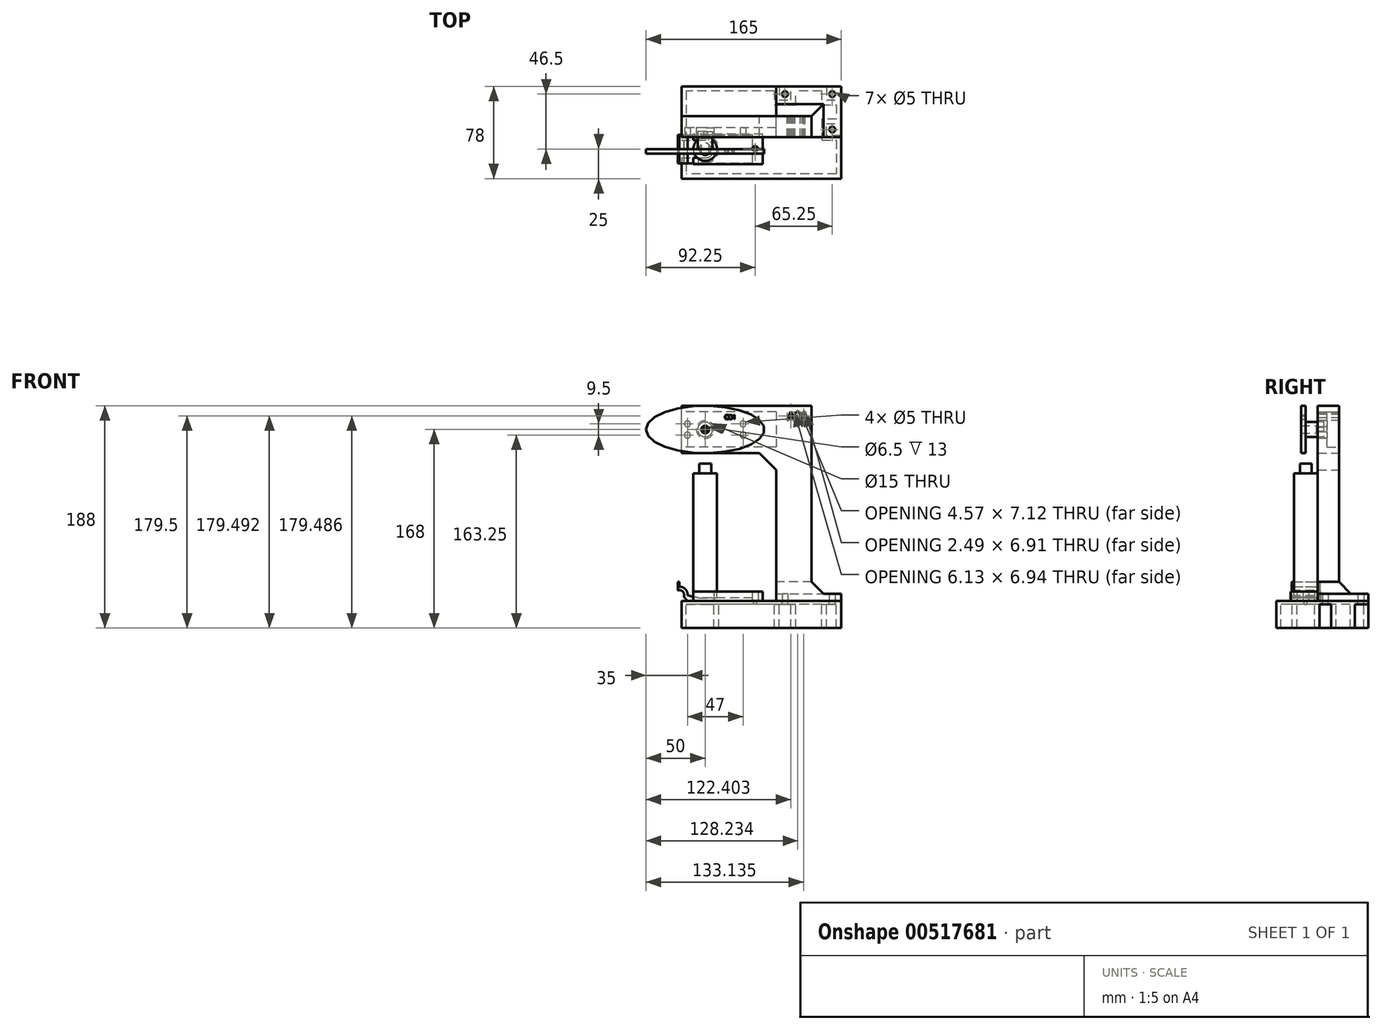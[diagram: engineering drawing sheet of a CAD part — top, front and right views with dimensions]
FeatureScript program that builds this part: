
annotation { "Feature Type Name" : "Feature", "Feature Type Description" : "" }
export const myFeature = defineFeature(function(context is Context, id is Id, definition is map)
    precondition{}
    {
        {
            var Q0;
            Q0=qCreatedBy(makeId("Front.planeOp"),FACE);
            var sketch = newSketch(context, id + "F0", { "sketchPlane" : qUnion([Q0])});
            skLineSegment(sketch, "E0", {"start": v(0, 0) * mm, "end": v(0, 110.86) * mm});
            skLineSegment(sketch, "E1", {"start": v(0, 110.86) * mm, "end": v(-14.14, 125) * mm});
            skLineSegment(sketch, "E2", {"start": v(-14.14, 125) * mm, "end": v(-80, 125) * mm});
            skLineSegment(sketch, "E3", {"start": v(-80, 125) * mm, "end": v(-80, 165) * mm});
            skLineSegment(sketch, "E4", {"start": v(-80, 165) * mm, "end": v(30, 165) * mm});
            skLineSegment(sketch, "E5", {"start": v(30, 165) * mm, "end": v(30, 0) * mm});
            skLineSegment(sketch, "E6", {"start": v(30, 0) * mm, "end": v(0, 0) * mm});
            skLineSegment(sketch, "E7", {"start": v(-14.14, 125) * mm, "end": v(0, 125) * mm, "construction": true});
            skLineSegment(sketch, "E8", {"start": v(0, 125) * mm, "end": v(0, 110.86) * mm, "construction": true});
            skText(sketch, "E9", { "text": "A01", "fontName": "OpenSans-Regular.ttf"});
            skLineSegment(sketch, "E10", {"start": v(25, 165) * mm, "end": v(25, 160) * mm, "construction": true});
            skLineSegment(sketch, "E11", {"start": v(25, 160) * mm, "end": v(30, 160) * mm, "construction": true});
            const initialGuessF0  = {"E9": [0.00934, 0.15303, 1, 0, 0.00697]};
            skSetInitialGuess(sketch, initialGuessF0);
            skSolve(sketch);
        }
        {
            var Q0;
            Q0=qSketchRegion(id+"F0",true);
            extrude(context, id + "F1", {"entities" : qUnion([Q0]), "depth" : 18 * mm, "offsetDistance" : 25 * mm});
        }
        {
            var Q0;
            Q0=makeQuery(id+"F1.opExtrude","CAP_FACE",FACE,{"disambiguationData":[OSD([sQuery(id+"F0.wireOp",EDGE,"E0"),sQuery(id+"F0.wireOp",EDGE,"E1"),sQuery(id+"F0.wireOp",EDGE,"E2"),sQuery(id+"F0.wireOp",EDGE,"E3"),sQuery(id+"F0.wireOp",EDGE,"E4"),sQuery(id+"F0.wireOp",EDGE,"E5"),sQuery(id+"F0.wireOp",EDGE,"E6")])],"isStart":false});
            var sketch = newSketch(context, id + "F2", { "sketchPlane" : qUnion([Q0])});
            skCircle(sketch, "E12", {"center": v(-75, 149.75) * mm, "radius": 2.5 * mm});
            skCircle(sketch, "E13", {"center": v(-75, 140.25) * mm, "radius": 2.5 * mm});
            skCircle(sketch, "E14", {"center": v(-28, 140.25) * mm, "radius": 2.5 * mm});
            skCircle(sketch, "E15", {"center": v(-28, 149.75) * mm, "radius": 2.5 * mm});
            skCircle(sketch, "E16", {"center": v(-60, 145) * mm, "radius": 7.5 * mm});
            skLineSegment(sketch, "E17", {"start": v(-75, 149.75) * mm, "end": v(-60, 149.75) * mm, "construction": true});
            skLineSegment(sketch, "E18", {"start": v(-60, 149.75) * mm, "end": v(-60, 145) * mm, "construction": true});
            skLineSegment(sketch, "E19", {"start": v(-75, 140.25) * mm, "end": v(-60, 140.25) * mm, "construction": true});
            skLineSegment(sketch, "E20", {"start": v(-60, 140.25) * mm, "end": v(-60, 145) * mm, "construction": true});
            skSolve(sketch);
        }
        {
            var Q0;
            Q0=qSketchRegion(id+"F2",true);
            extrude(context, id + "F3", {"entities" : qUnion([Q0]), "operationType" : NewBodyOperationType.REMOVE, "endBound" : BoundingType.THROUGH_ALL, "oppositeDirection" : true, "depth" : 25 * mm, "offsetDistance" : 25 * mm});
        }
        {
            var Q0;
            Q0=makeQuery(id+"F1.opExtrude","CAP_FACE",FACE,{"disambiguationData":[OSD([sQuery(id+"F0.wireOp",EDGE,"E0"),sQuery(id+"F0.wireOp",EDGE,"E1"),sQuery(id+"F0.wireOp",EDGE,"E2"),sQuery(id+"F0.wireOp",EDGE,"E3"),sQuery(id+"F0.wireOp",EDGE,"E4"),sQuery(id+"F0.wireOp",EDGE,"E5"),sQuery(id+"F0.wireOp",EDGE,"E6")])],"isStart":true});
            var sketch = newSketch(context, id + "F4", { "sketchPlane" : qUnion([Q0])});
            skLineSegment(sketch, "E21.bottom", {"start": v(0, 160) * mm, "end": v(80, 160) * mm});
            skLineSegment(sketch, "E21.top", {"start": v(0, 130) * mm, "end": v(80, 130) * mm});
            skLineSegment(sketch, "E21.left", {"start": v(0, 160) * mm, "end": v(0, 130) * mm});
            skLineSegment(sketch, "E21.right", {"start": v(80, 160) * mm, "end": v(80, 130) * mm});
            skSolve(sketch);
        }
        {
            var Q0;
            Q0=qSketchRegion(id+"F4",true);
            extrude(context, id + "F5", {"entities" : qUnion([Q0]), "operationType" : NewBodyOperationType.REMOVE, "oppositeDirection" : true, "depth" : 10 * mm, "offsetDistance" : 25 * mm});
        }
        {
            var Q0;
            Q0=qCreatedBy(makeId("Top.planeOp"),FACE);
            var sketch = newSketch(context, id + "F6", { "sketchPlane" : qUnion([Q0])});
            skLineSegment(sketch, "E22.top", {"start": v(0, 25) * mm, "end": v(55, 25) * mm});
            skLineSegment(sketch, "E22.right", {"start": v(55, -18) * mm, "end": v(55, 25) * mm});
            skCircle(sketch, "E23", {"center": v(7.5, 18.5) * mm, "radius": 2.5 * mm});
            skCircle(sketch, "E24", {"center": v(47.5, 18.5) * mm, "radius": 2.5 * mm});
            skCircle(sketch, "E25", {"center": v(47.5, -11.5) * mm, "radius": 2.5 * mm});
            skLineSegment(sketch, "E26", {"start": v(0, -18) * mm, "end": v(30, -18) * mm});
            skLineSegment(sketch, "E27", {"start": v(30, -18) * mm, "end": v(55, -18) * mm});
            skLineSegment(sketch, "E28", {"start": v(0, -18) * mm, "end": v(0, 0) * mm});
            skLineSegment(sketch, "E29", {"start": v(0, 0) * mm, "end": v(0, 25) * mm});
            skLineSegment(sketch, "E30", {"start": v(0, 18.5) * mm, "end": v(7.5, 18.5) * mm, "construction": true});
            skLineSegment(sketch, "E31", {"start": v(47.5, 18.5) * mm, "end": v(55, 18.5) * mm, "construction": true});
            skLineSegment(sketch, "E32", {"start": v(47.5, -11.5) * mm, "end": v(47.5, -18) * mm, "construction": true});
            skLineSegment(sketch, "E33", {"start": v(47.5, 18.5) * mm, "end": v(47.5, 25) * mm, "construction": true});
            skSolve(sketch);
        }
        {
            var Q0;
            Q0=qSketchRegion(id+"F6",true);
            extrude(context, id + "F7", {"entities" : qUnion([Q0]), "operationType" : NewBodyOperationType.ADD, "depth" : 6 * mm, "offsetDistance" : 25 * mm});
        }
        {
            var Q0;
            Q0=makeQuery(id+"F7.boolean.opBoolean","INTERSECT",EDGE,{"derivedFrom":[makeQuery(id+"F1.opExtrude","SWEPT_FACE",FACE,{"disambiguationData":[OSD([sQuery(id+"F0.wireOp",EDGE,"E5")])]}),makeQuery(id+"F7.opExtrude","CAP_FACE",FACE,{"disambiguationData":[OSD([sQuery(id+"F6.wireOp",EDGE,"E22.top"),sQuery(id+"F6.wireOp",EDGE,"E22.right"),sQuery(id+"F6.wireOp",EDGE,"E23"),sQuery(id+"F6.wireOp",EDGE,"E24"),sQuery(id+"F6.wireOp",EDGE,"E25"),sQuery(id+"F6.wireOp",EDGE,"E26"),sQuery(id+"F6.wireOp",EDGE,"E27"),sQuery(id+"F6.wireOp",EDGE,"E28"),sQuery(id+"F6.wireOp",EDGE,"E29")])],"isStart":false})]});
            var Q1;
            Q1=makeQuery(id+"F7.boolean.opBoolean","INTERSECT",EDGE,{"derivedFrom":[makeQuery(id+"F1.opExtrude","CAP_FACE",FACE,{"disambiguationData":[OSD([sQuery(id+"F0.wireOp",EDGE,"E0"),sQuery(id+"F0.wireOp",EDGE,"E1"),sQuery(id+"F0.wireOp",EDGE,"E2"),sQuery(id+"F0.wireOp",EDGE,"E3"),sQuery(id+"F0.wireOp",EDGE,"E4"),sQuery(id+"F0.wireOp",EDGE,"E5"),sQuery(id+"F0.wireOp",EDGE,"E6"),sQuery(id+"F0.wireOp",EDGE,"E9.sketch_text.stroke-0"),sQuery(id+"F0.wireOp",EDGE,"E9.sketch_text.stroke-1"),sQuery(id+"F0.wireOp",EDGE,"E9.sketch_text.stroke-2"),sQuery(id+"F0.wireOp",EDGE,"E9.sketch_text.stroke-3"),sQuery(id+"F0.wireOp",EDGE,"E9.sketch_text.stroke-4"),sQuery(id+"F0.wireOp",EDGE,"E9.sketch_text.stroke-5"),sQuery(id+"F0.wireOp",EDGE,"E9.sketch_text.stroke-6"),sQuery(id+"F0.wireOp",EDGE,"E9.sketch_text.stroke-7"),sQuery(id+"F0.wireOp",EDGE,"E9.sketch_text.stroke-13"),sQuery(id+"F0.wireOp",EDGE,"E9.sketch_text.stroke-14"),sQuery(id+"F0.wireOp",EDGE,"E9.sketch_text.stroke-15"),sQuery(id+"F0.wireOp",EDGE,"E9.sketch_text.stroke-16"),sQuery(id+"F0.wireOp",EDGE,"E9.sketch_text.stroke-17"),sQuery(id+"F0.wireOp",EDGE,"E9.sketch_text.stroke-18"),sQuery(id+"F0.wireOp",EDGE,"E9.sketch_text.stroke-19"),sQuery(id+"F0.wireOp",EDGE,"E9.sketch_text.stroke-20"),sQuery(id+"F0.wireOp",EDGE,"E9.sketch_text.stroke-29"),sQuery(id+"F0.wireOp",EDGE,"E9.sketch_text.stroke-30"),sQuery(id+"F0.wireOp",EDGE,"E9.sketch_text.stroke-31"),sQuery(id+"F0.wireOp",EDGE,"E9.sketch_text.stroke-32"),sQuery(id+"F0.wireOp",EDGE,"E9.sketch_text.stroke-33"),sQuery(id+"F0.wireOp",EDGE,"E9.sketch_text.stroke-34"),sQuery(id+"F0.wireOp",EDGE,"E9.sketch_text.stroke-35"),sQuery(id+"F0.wireOp",EDGE,"E9.sketch_text.stroke-36"),sQuery(id+"F0.wireOp",EDGE,"E9.sketch_text.stroke-37")])],"isStart":true}),makeQuery(id+"F7.opExtrude","CAP_FACE",FACE,{"disambiguationData":[OSD([sQuery(id+"F6.wireOp",EDGE,"E22.top"),sQuery(id+"F6.wireOp",EDGE,"E22.right"),sQuery(id+"F6.wireOp",EDGE,"E23"),sQuery(id+"F6.wireOp",EDGE,"E24"),sQuery(id+"F6.wireOp",EDGE,"E25"),sQuery(id+"F6.wireOp",EDGE,"E26"),sQuery(id+"F6.wireOp",EDGE,"E27"),sQuery(id+"F6.wireOp",EDGE,"E28"),sQuery(id+"F6.wireOp",EDGE,"E29")])],"isStart":false})]});
            chamfer(context, id + "F8", {"entities" : qUnion([Q0, Q1]), "width" : 10 * mm, "tangentPropagation" : true});
        }
        {
            var Q0;
            Q0=makeQuery(id+"F1.opExtrude","CAP_FACE",FACE,{"disambiguationData":[OSD([sQuery(id+"F0.wireOp",EDGE,"E0"),sQuery(id+"F0.wireOp",EDGE,"E1"),sQuery(id+"F0.wireOp",EDGE,"E2"),sQuery(id+"F0.wireOp",EDGE,"E3"),sQuery(id+"F0.wireOp",EDGE,"E4"),sQuery(id+"F0.wireOp",EDGE,"E5"),sQuery(id+"F0.wireOp",EDGE,"E6")])],"isStart":false});
            cPlane(context, id + "F9", {"entities" : qUnion([Q0]), "cplaneType" : CPlaneType.OFFSET, "offset" : 10 * mm, "width" : 150 * mm, "height" : 150 * mm});
        }
        {
            var Q0;
            Q0=qCreatedBy(id+"F9.planeOp",FACE);
            var sketch = newSketch(context, id + "F10", { "sketchPlane" : qUnion([Q0])});
            skEllipse(sketch, "E34", {"center": v(-60, 145) * mm, "majorRadius": 50 * mm, "minorRadius": 20 * mm, "majorAxis": v(-1, 0)});
            skCircle(sketch, "E35", {"center": v(-60, 145) * mm, "radius": 3.25 * mm});
            skText(sketch, "E36", { "text": "C01", "fontName": "OpenSans-Regular.ttf"});
            skLineSegment(sketch, "E37", {"start": v(-60, 145) * mm, "end": v(-10, 145) * mm, "construction": true});
            const initialGuessF10  = {"E36": [-0.04367, 0.1535, 1, 0, 0.004]};
            skSetInitialGuess(sketch, initialGuessF10);
            skSolve(sketch);
        }
        {
            var Q0;
            Q0=qSketchRegion(id+"F10",true);
            extrude(context, id + "F11", {"entities" : qUnion([Q0]), "depth" : 4 * mm, "offsetDistance" : 25 * mm});
        }
        {
            var Q0;
            Q0=makeQuery(id+"F11.opExtrude","CAP_FACE",FACE,{"disambiguationData":[OSD([sQuery(id+"F10.wireOp",EDGE,"E34"),sQuery(id+"F10.wireOp",EDGE,"E35"),sQuery(id+"F10.wireOp",EDGE,"E36.sketch_text.stroke-0"),sQuery(id+"F10.wireOp",EDGE,"E36.sketch_text.stroke-1"),sQuery(id+"F10.wireOp",EDGE,"E36.sketch_text.stroke-2"),sQuery(id+"F10.wireOp",EDGE,"E36.sketch_text.stroke-3"),sQuery(id+"F10.wireOp",EDGE,"E36.sketch_text.stroke-4"),sQuery(id+"F10.wireOp",EDGE,"E36.sketch_text.stroke-5"),sQuery(id+"F10.wireOp",EDGE,"E36.sketch_text.stroke-6"),sQuery(id+"F10.wireOp",EDGE,"E36.sketch_text.stroke-7"),sQuery(id+"F10.wireOp",EDGE,"E36.sketch_text.stroke-8"),sQuery(id+"F10.wireOp",EDGE,"E36.sketch_text.stroke-9"),sQuery(id+"F10.wireOp",EDGE,"E36.sketch_text.stroke-10"),sQuery(id+"F10.wireOp",EDGE,"E36.sketch_text.stroke-11"),sQuery(id+"F10.wireOp",EDGE,"E36.sketch_text.stroke-12"),sQuery(id+"F10.wireOp",EDGE,"E36.sketch_text.stroke-13"),sQuery(id+"F10.wireOp",EDGE,"E36.sketch_text.stroke-14"),sQuery(id+"F10.wireOp",EDGE,"E36.sketch_text.stroke-15"),sQuery(id+"F10.wireOp",EDGE,"E36.sketch_text.stroke-16"),sQuery(id+"F10.wireOp",EDGE,"E36.sketch_text.stroke-17"),sQuery(id+"F10.wireOp",EDGE,"E36.sketch_text.stroke-18"),sQuery(id+"F10.wireOp",EDGE,"E36.sketch_text.stroke-19"),sQuery(id+"F10.wireOp",EDGE,"E36.sketch_text.stroke-20"),sQuery(id+"F10.wireOp",EDGE,"E36.sketch_text.stroke-21"),sQuery(id+"F10.wireOp",EDGE,"E36.sketch_text.stroke-22"),sQuery(id+"F10.wireOp",EDGE,"E36.sketch_text.stroke-31"),sQuery(id+"F10.wireOp",EDGE,"E36.sketch_text.stroke-32"),sQuery(id+"F10.wireOp",EDGE,"E36.sketch_text.stroke-33"),sQuery(id+"F10.wireOp",EDGE,"E36.sketch_text.stroke-34"),sQuery(id+"F10.wireOp",EDGE,"E36.sketch_text.stroke-35"),sQuery(id+"F10.wireOp",EDGE,"E36.sketch_text.stroke-36"),sQuery(id+"F10.wireOp",EDGE,"E36.sketch_text.stroke-37"),sQuery(id+"F10.wireOp",EDGE,"E36.sketch_text.stroke-38"),sQuery(id+"F10.wireOp",EDGE,"E36.sketch_text.stroke-39")])],"isStart":true});
            var sketch = newSketch(context, id + "F12", { "sketchPlane" : qUnion([Q0])});
            skCircle(sketch, "E38", {"center": v(60, 145) * mm, "radius": 3.25 * mm});
            skCircle(sketch, "E39", {"center": v(60, 145) * mm, "radius": 6.25 * mm});
            skSolve(sketch);
        }
        {
            var Q0;
            Q0=qSketchRegion(id+"F12",true);
            extrude(context, id + "F13", {"entities" : qUnion([Q0]), "operationType" : NewBodyOperationType.ADD, "depth" : 9 * mm, "offsetDistance" : 25 * mm});
        }
        {
            var Q0;
            Q0=makeQuery(id+"F13.opExtrude","CAP_FACE",FACE,{"disambiguationData":[OSD([sQuery(id+"F12.wireOp",EDGE,"E38"),sQuery(id+"F12.wireOp",EDGE,"E39")])],"isStart":false});
            var sketch = newSketch(context, id + "F14", { "sketchPlane" : qUnion([Q0])});
            skCircle(sketch, "E40", {"center": v(60, 145) * mm, "radius": 6.25 * mm});
            skCircle(sketch, "E41", {"center": v(60, 145) * mm, "radius": 1.5 * mm});
            skSolve(sketch);
        }
        {
            var Q0;
            Q0=qSketchRegion(id+"F14",true);
            extrude(context, id + "F15", {"entities" : qUnion([Q0]), "operationType" : NewBodyOperationType.ADD, "depth" : 6 * mm, "offsetDistance" : 25 * mm});
        }
        {
            var Q0;
            Q0=qCreatedBy(id+"F9.planeOp",FACE);
            var sketch = newSketch(context, id + "F16", { "sketchPlane" : qUnion([Q0])});
            skLineSegment(sketch, "E42.bottom", {"start": v(-60, 116) * mm, "end": v(-55, 116) * mm});
            skLineSegment(sketch, "E42.top", {"start": v(-60, 0) * mm, "end": v(-55, 0) * mm});
            skLineSegment(sketch, "E42.left", {"start": v(-60, 116) * mm, "end": v(-60, 0) * mm});
            skLineSegment(sketch, "E42.right", {"start": v(-55, 116) * mm, "end": v(-55, 0) * mm});
            skLineSegment(sketch, "E43.bottom", {"start": v(-55, 108) * mm, "end": v(-50, 108) * mm});
            skLineSegment(sketch, "E43.top", {"start": v(-55, 0) * mm, "end": v(-50, 0) * mm});
            skLineSegment(sketch, "E43.left", {"start": v(-55, 108) * mm, "end": v(-55, 0) * mm});
            skLineSegment(sketch, "E43.right", {"start": v(-50, 108) * mm, "end": v(-50, 0) * mm});
            skLineSegment(sketch, "E44", {"start": v(-60, 145) * mm, "end": v(-60, 116) * mm, "construction": true});
            skSolve(sketch);
        }
        {
            var Q0;
            Q0=qSketchRegion(id+"F16",true);
            var Q1;
            Q1=sQuery(id+"F16.wireOp",EDGE,"E42.left");
            revolve(context, id + "F17", {"entities" : qUnion([Q0]), "axis" : qUnion([Q1]), "revolveType" : RevolveType.FULL});
        }
        {
            var Q0;
            Q0=qCreatedBy(id+"F9.planeOp",FACE);
            var sketch = newSketch(context, id + "F18", { "sketchPlane" : qUnion([Q0])});
            skLineSegment(sketch, "E45", {"start": v(-75, 0) * mm, "end": v(-20, 0) * mm});
            skLineSegment(sketch, "E46", {"start": v(-20, 0) * mm, "end": v(-20, 2.5) * mm});
            skLineSegment(sketch, "E47", {"start": v(-20, 2.5) * mm, "end": v(-65.74, 2.5) * mm});
            skLineSegment(sketch, "E48", {"start": v(-65.74, 2.5) * mm, "end": v(-74.78, 4.68) * mm});
            skArc(sketch, "E49", {"start": v(-74.78, 4.68) * mm, "mid": v(-76.75, 9.88) * mm, "end": v(-81.9, 12) * mm});
            skLineSegment(sketch, "E50", {"start": v(-81.9, 12) * mm, "end": v(-81.9, 16.06) * mm});
            skLineSegment(sketch, "E51", {"start": v(-81.9, 16.06) * mm, "end": v(-83, 16.06) * mm});
            skLineSegment(sketch, "E52", {"start": v(-83, 16.06) * mm, "end": v(-83, 8.8) * mm});
            skArc(sketch, "E53", {"start": v(-78.13, 3.33) * mm, "mid": v(-78.78, 7.66) * mm, "end": v(-83, 8.8) * mm});
            skLineSegment(sketch, "E54", {"start": v(-78.13, 3.33) * mm, "end": v(-75, 0) * mm});
            skLineSegment(sketch, "E55", {"start": v(-60, 0) * mm, "end": v(-60, 108) * mm, "construction": true});
            skSolve(sketch);
        }
        {
            var Q0;
            Q0=makeQuery(id+"F18.imprint","IMPRINT",FACE,{"disambiguationData":[TD([[makeQuery(id+"F18.imprint","IMPRINT",EDGE,{"derivedFrom":sQuery(id+"F18.wireOp",EDGE,"E45")}),1.0]])]});
            extrude(context, id + "F19", {"entities" : qUnion([Q0]), "operationType" : NewBodyOperationType.ADD, "endBound" : BoundingType.SYMMETRIC, "depth" : 24 * mm, "offsetDistance" : 25 * mm});
        }
        {
            var Q0;
            Q0=qCreatedBy(makeId("Top.planeOp"),FACE);
            var sketch = newSketch(context, id + "F20", { "sketchPlane" : qUnion([Q0])});
            skLineSegment(sketch, "E56.bottom", {"start": v(55, 25) * mm, "end": v(-80, 25) * mm});
            skLineSegment(sketch, "E56.top", {"start": v(55, -53) * mm, "end": v(-80, -53) * mm});
            skLineSegment(sketch, "E56.left", {"start": v(55, 25) * mm, "end": v(55, -53) * mm});
            skLineSegment(sketch, "E56.right", {"start": v(-80, 25) * mm, "end": v(-80, -20.5) * mm});
            skLineSegment(sketch, "E57", {"start": v(-80, -35.5) * mm, "end": v(-60, -35.5) * mm});
            skLineSegment(sketch, "E58", {"start": v(-80, -20.5) * mm, "end": v(-60, -20.5) * mm});
            skArc(sketch, "E59", {"start": v(-60, -35.5) * mm, "mid": v(-52.5, -28) * mm, "end": v(-60, -20.5) * mm});
            skLineSegment(sketch, "E60.trimOffspring", {"start": v(-80, -35.5) * mm, "end": v(-80, -53) * mm});
            skLineSegment(sketch, "E61", {"start": v(-80, -35.5) * mm, "end": v(-80, -20.5) * mm, "construction": true});
            skCircle(sketch, "E62", {"center": v(7.5, 18.5) * mm, "radius": 2.5 * mm});
            skCircle(sketch, "E63", {"center": v(47.5, 18.5) * mm, "radius": 2.5 * mm});
            skCircle(sketch, "E64", {"center": v(47.5, -11.5) * mm, "radius": 2.5 * mm});
            skLineSegment(sketch, "E65", {"start": v(-60, -28) * mm, "end": v(-19, -28) * mm, "construction": true});
            skCircle(sketch, "E66", {"center": v(-17.75, -28) * mm, "radius": 1.25 * mm});
            skSolve(sketch);
        }
        {
            var Q0;
            Q0=qSketchRegion(id+"F20",true);
            extrude(context, id + "F21", {"entities" : qUnion([Q0]), "oppositeDirection" : true, "depth" : 3 * mm, "offsetDistance" : 25 * mm});
        }
        {
            var Q0;
            Q0=makeQuery(id+"F21.opExtrude","CAP_FACE",FACE,{"disambiguationData":[OSD([sQuery(id+"F20.wireOp",EDGE,"E56.bottom"),sQuery(id+"F20.wireOp",EDGE,"E56.top"),sQuery(id+"F20.wireOp",EDGE,"E56.left"),sQuery(id+"F20.wireOp",EDGE,"E56.right"),sQuery(id+"F20.wireOp",EDGE,"E57"),sQuery(id+"F20.wireOp",EDGE,"E58"),sQuery(id+"F20.wireOp",EDGE,"E59"),sQuery(id+"F20.wireOp",EDGE,"E60.trimOffspring"),sQuery(id+"F20.wireOp",EDGE,"E62"),sQuery(id+"F20.wireOp",EDGE,"E63"),sQuery(id+"F20.wireOp",EDGE,"E64")])],"isStart":false});
            var sketch = newSketch(context, id + "F22", { "sketchPlane" : qUnion([Q0])});
            skLineSegment(sketch, "E67.0", {"start": v(38.5, -21) * mm, "end": v(16.5, -21) * mm});
            skLineSegment(sketch, "E67.1", {"start": v(51, -9.5) * mm, "end": v(51, 2.5) * mm});
            skLineSegment(sketch, "E67.2", {"start": v(-76, -21) * mm, "end": v(-76, 16.5) * mm});
            skLineSegment(sketch, "E67.3", {"start": v(51, 49) * mm, "end": v(-76, 49) * mm});
            skLineSegment(sketch, "E67.4", {"start": v(-76, 16.5) * mm, "end": v(-60, 16.5) * mm});
            skArc(sketch, "E67.5", {"start": v(-60, 39.5) * mm, "mid": v(-48.5, 28) * mm, "end": v(-60, 16.5) * mm});
            skLineSegment(sketch, "E67.6", {"start": v(-76, 39.5) * mm, "end": v(-60, 39.5) * mm});
            skLineSegment(sketch, "E67.7", {"start": v(-76, 39.5) * mm, "end": v(-76, 49) * mm});
            skLineSegment(sketch, "E68.trimOffspring", {"start": v(-1.5, -21) * mm, "end": v(-76, -21) * mm});
            skLineSegment(sketch, "E69.trimOffspring", {"start": v(51, 20.5) * mm, "end": v(51, 49) * mm});
            skLineSegment(sketch, "E70", {"start": v(2.5, -25) * mm, "end": v(-80, -25) * mm});
            skLineSegment(sketch, "E71", {"start": v(-80, -25) * mm, "end": v(-80, 20.5) * mm});
            skLineSegment(sketch, "E72", {"start": v(-80, 20.5) * mm, "end": v(-60, 20.5) * mm});
            skLineSegment(sketch, "E73", {"start": v(-60, 35.5) * mm, "end": v(-80, 35.5) * mm});
            skLineSegment(sketch, "E74", {"start": v(-80, 35.5) * mm, "end": v(-80, 53) * mm});
            skLineSegment(sketch, "E75", {"start": v(-80, 53) * mm, "end": v(55, 53) * mm});
            skLineSegment(sketch, "E76", {"start": v(55, 53) * mm, "end": v(55, 16.5) * mm});
            skLineSegment(sketch, "E77", {"start": v(55, 6.5) * mm, "end": v(55, -13.5) * mm});
            skLineSegment(sketch, "E78", {"start": v(42.5, -25) * mm, "end": v(12.5, -25) * mm});
            skArc(sketch, "E79", {"start": v(-60, 20.5) * mm, "mid": v(-52.5, 28) * mm, "end": v(-60, 35.5) * mm});
            skLineSegment(sketch, "E80", {"start": v(2.5, -25) * mm, "end": v(2.5, -13.5) * mm});
            skLineSegment(sketch, "E81", {"start": v(2.5, -13.5) * mm, "end": v(12.5, -13.5) * mm});
            skLineSegment(sketch, "E82", {"start": v(12.5, -13.5) * mm, "end": v(12.5, -25) * mm});
            skLineSegment(sketch, "E83", {"start": v(-1.5, -21) * mm, "end": v(-1.5, -9.5) * mm});
            skLineSegment(sketch, "E84", {"start": v(-1.5, -9.5) * mm, "end": v(16.5, -9.5) * mm});
            skLineSegment(sketch, "E85", {"start": v(16.5, -9.5) * mm, "end": v(16.5, -21) * mm});
            skLineSegment(sketch, "E86", {"start": v(38.5, -21) * mm, "end": v(38.5, -9.5) * mm});
            skLineSegment(sketch, "E87", {"start": v(38.5, -9.5) * mm, "end": v(51, -9.5) * mm});
            skLineSegment(sketch, "E88", {"start": v(42.5, -25) * mm, "end": v(42.5, -13.5) * mm});
            skLineSegment(sketch, "E89", {"start": v(42.5, -13.5) * mm, "end": v(55, -13.5) * mm});
            skLineSegment(sketch, "E90", {"start": v(51, 2.5) * mm, "end": v(38.5, 2.5) * mm});
            skLineSegment(sketch, "E91", {"start": v(38.5, 2.5) * mm, "end": v(38.5, 20.5) * mm});
            skLineSegment(sketch, "E92", {"start": v(38.5, 20.5) * mm, "end": v(51, 20.5) * mm});
            skLineSegment(sketch, "E93", {"start": v(55, 16.5) * mm, "end": v(42.5, 16.5) * mm});
            skLineSegment(sketch, "E94", {"start": v(42.5, 16.5) * mm, "end": v(42.5, 6.5) * mm});
            skLineSegment(sketch, "E95", {"start": v(42.5, 6.5) * mm, "end": v(55, 6.5) * mm});
            skLineSegment(sketch, "E96", {"start": v(-1.5, -13.5) * mm, "end": v(2.5, -13.5) * mm, "construction": true});
            skLineSegment(sketch, "E97", {"start": v(2.5, -9.5) * mm, "end": v(2.5, -13.5) * mm, "construction": true});
            skLineSegment(sketch, "E98", {"start": v(12.5, -13.5) * mm, "end": v(12.5, -9.5) * mm, "construction": true});
            skLineSegment(sketch, "E99", {"start": v(12.5, -13.5) * mm, "end": v(16.5, -13.5) * mm, "construction": true});
            skLineSegment(sketch, "E100", {"start": v(12.5, -21) * mm, "end": v(16.5, -21) * mm, "construction": true});
            skLineSegment(sketch, "E101", {"start": v(16.5, -21) * mm, "end": v(16.5, -25) * mm, "construction": true});
            skLineSegment(sketch, "E102", {"start": v(38.5, -25) * mm, "end": v(38.5, -21) * mm, "construction": true});
            skLineSegment(sketch, "E103", {"start": v(38.5, -21) * mm, "end": v(42.5, -21) * mm, "construction": true});
            skLineSegment(sketch, "E104", {"start": v(38.5, -13.5) * mm, "end": v(42.5, -13.5) * mm, "construction": true});
            skLineSegment(sketch, "E105", {"start": v(42.5, -9.5) * mm, "end": v(42.5, -13.5) * mm, "construction": true});
            skLineSegment(sketch, "E106", {"start": v(51, -13.5) * mm, "end": v(51, -9.5) * mm, "construction": true});
            skLineSegment(sketch, "E107", {"start": v(55, -9.5) * mm, "end": v(51, -9.5) * mm, "construction": true});
            skLineSegment(sketch, "E108", {"start": v(55, 2.5) * mm, "end": v(51, 2.5) * mm, "construction": true});
            skLineSegment(sketch, "E109", {"start": v(51, 6.5) * mm, "end": v(51, 2.5) * mm, "construction": true});
            skLineSegment(sketch, "E110", {"start": v(42.5, 2.5) * mm, "end": v(42.5, 6.5) * mm, "construction": true});
            skLineSegment(sketch, "E111", {"start": v(38.5, 6.5) * mm, "end": v(42.5, 6.5) * mm, "construction": true});
            skLineSegment(sketch, "E112", {"start": v(42.5, 20.5) * mm, "end": v(42.5, 16.5) * mm, "construction": true});
            skLineSegment(sketch, "E113", {"start": v(38.5, 16.5) * mm, "end": v(42.5, 16.5) * mm, "construction": true});
            skLineSegment(sketch, "E114", {"start": v(51, 16.5) * mm, "end": v(51, 20.5) * mm, "construction": true});
            skLineSegment(sketch, "E115", {"start": v(51, 20.5) * mm, "end": v(55, 20.5) * mm, "construction": true});
            skCircle(sketch, "E116", {"center": v(7.5, -18.5) * mm, "radius": 5 * mm, "construction": true});
            skCircle(sketch, "E117", {"center": v(47.5, -18.5) * mm, "radius": 5 * mm, "construction": true});
            skCircle(sketch, "E118", {"center": v(47.5, 11.5) * mm, "radius": 5 * mm, "construction": true});
            skSolve(sketch);
        }
        {
            var Q0;
            Q0 = qSketchRegion(id + "F22", true);
            extrude(context, id + "F23", {"entities" : qUnion([Q0]), "operationType" : NewBodyOperationType.ADD, "depth" : 20 * mm, "offsetDistance" : 25 * mm});
        }
        {
            var Q0;
            Q0=makeQuery(id+"F21.opExtrude","CAP_FACE",FACE,{"disambiguationData":[OSD([sQuery(id+"F20.wireOp",EDGE,"E56.bottom"),sQuery(id+"F20.wireOp",EDGE,"E56.top"),sQuery(id+"F20.wireOp",EDGE,"E56.left"),sQuery(id+"F20.wireOp",EDGE,"E56.right"),sQuery(id+"F20.wireOp",EDGE,"E57"),sQuery(id+"F20.wireOp",EDGE,"E58"),sQuery(id+"F20.wireOp",EDGE,"E59"),sQuery(id+"F20.wireOp",EDGE,"E60.trimOffspring"),sQuery(id+"F20.wireOp",EDGE,"E62"),sQuery(id+"F20.wireOp",EDGE,"E63"),sQuery(id+"F20.wireOp",EDGE,"E64"),sQuery(id+"F20.wireOp",EDGE,"E66")])],"isStart":true});
            var sketch = newSketch(context, id + "F24", { "sketchPlane" : qUnion([Q0])});
            skLineSegment(sketch, "E119", {"start": v(-70, -35.5) * mm, "end": v(-70, -40.7) * mm});
            skLineSegment(sketch, "E120", {"start": v(-70, -40.7) * mm, "end": v(-11.25, -40.7) * mm});
            skLineSegment(sketch, "E121", {"start": v(-11.25, -40.7) * mm, "end": v(-11.25, -15.3) * mm});
            skLineSegment(sketch, "E122", {"start": v(-11.25, -15.3) * mm, "end": v(-70, -15.3) * mm});
            skLineSegment(sketch, "E123", {"start": v(-70, -15.3) * mm, "end": v(-70, -20.5) * mm});
            skLineSegment(sketch, "E124", {"start": v(-70, -20.5) * mm, "end": v(-60, -20.5) * mm});
            skArc(sketch, "E125", {"start": v(-60, -35.5) * mm, "mid": v(-52.5, -28) * mm, "end": v(-60, -20.5) * mm});
            skLineSegment(sketch, "E126", {"start": v(-60, -35.5) * mm, "end": v(-70, -35.5) * mm});
            skCircle(sketch, "E127", {"center": v(-17.75, -28) * mm, "radius": 2.5 * mm});
            skSolve(sketch);
        }
        {
            var Q0;
            Q0=makeQuery(id+"F24.imprint","IMPRINT",FACE,{"disambiguationData":[TD([[makeQuery(id+"F24.imprint","IMPRINT",EDGE,{"derivedFrom":sQuery(id+"F24.wireOp",EDGE,"E119")}),1.0]])]});
            extrude(context, id + "F25", {"entities" : qUnion([Q0]), "depth" : 8 * mm, "offsetDistance" : 25 * mm});
        }
    });
